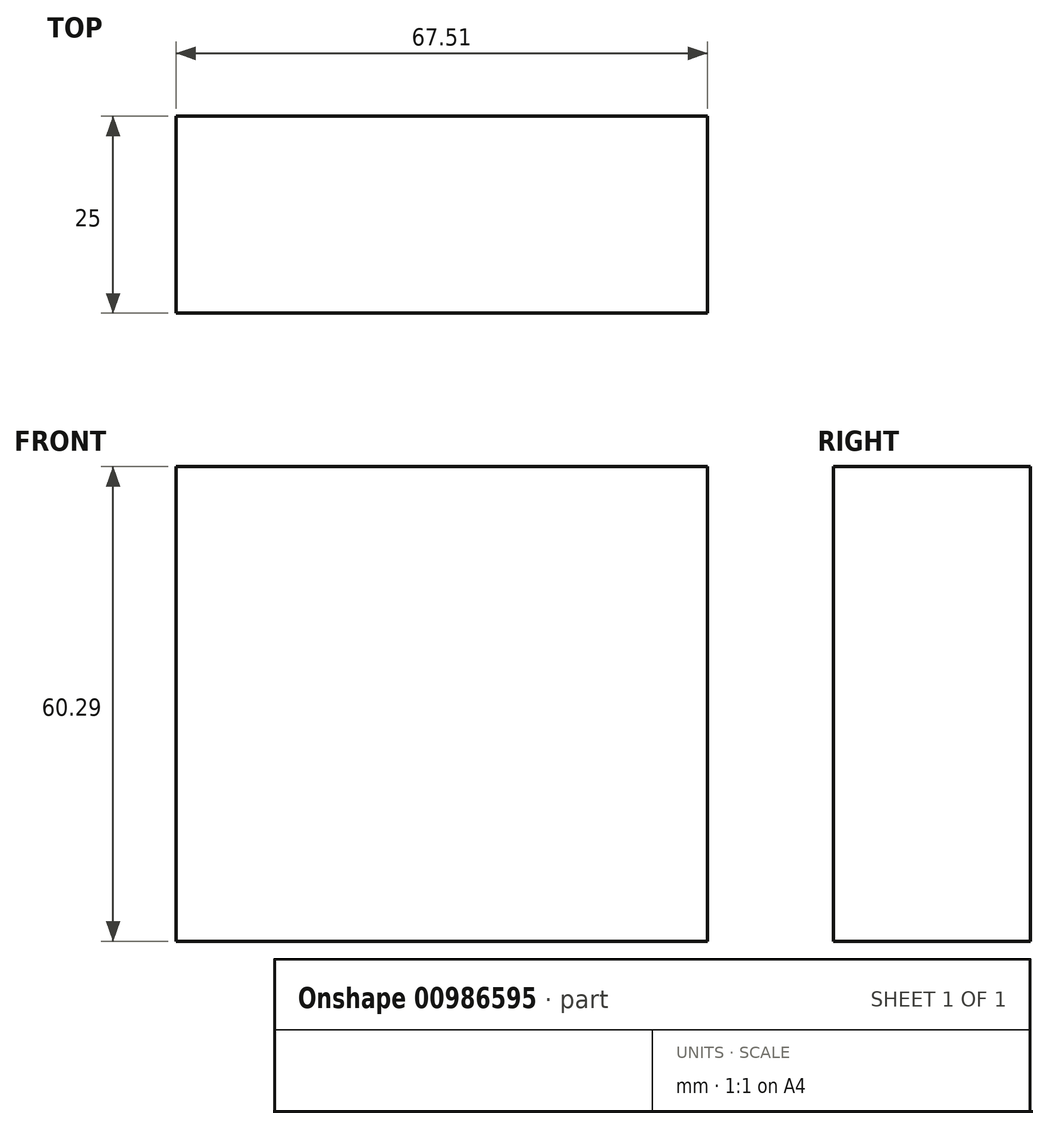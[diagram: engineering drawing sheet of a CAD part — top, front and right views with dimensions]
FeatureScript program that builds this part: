
annotation { "Feature Type Name" : "Feature", "Feature Type Description" : "" }
export const myFeature = defineFeature(function(context is Context, id is Id, definition is map)
    precondition{}
    {
        {
            var Q0;
            Q0=qCreatedBy(makeId("Front.planeOp"),FACE);
            var sketch = newSketch(context, id + "F0", { "sketchPlane" : qUnion([Q0])});
            skLineSegment(sketch, "E0.bottom", {"start": v(-115.29, 43.43) * mm, "end": v(-47.78, 43.43) * mm});
            skLineSegment(sketch, "E0.top", {"start": v(-115.29, -16.86) * mm, "end": v(-47.78, -16.86) * mm});
            skLineSegment(sketch, "E0.left", {"start": v(-115.29, 43.43) * mm, "end": v(-115.29, -16.86) * mm});
            skLineSegment(sketch, "E0.right", {"start": v(-47.78, 43.43) * mm, "end": v(-47.78, -16.86) * mm});
            skSolve(sketch);
        }
        {
            var Q0;
            Q0 = qSketchRegion(id + "F0", true);
            extrude(context, id + "F1", {"entities" : qUnion([Q0]), "depth" : 25 * mm, "offsetDistance" : 25 * mm});
        }
    });
